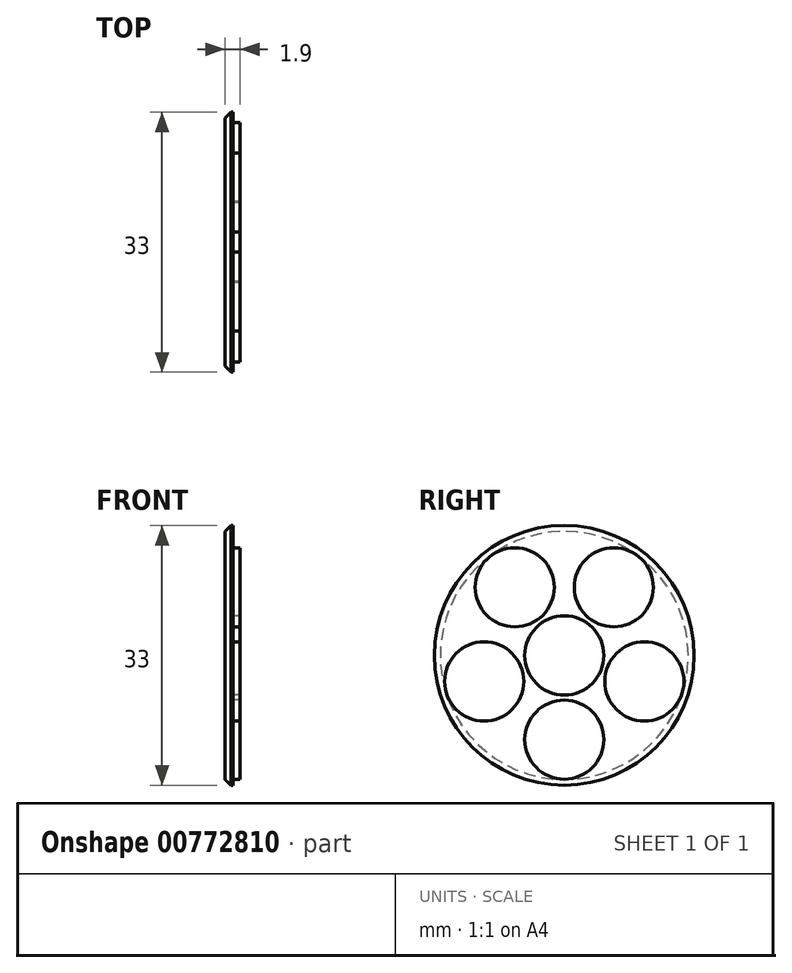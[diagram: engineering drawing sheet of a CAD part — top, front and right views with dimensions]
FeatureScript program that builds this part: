
annotation { "Feature Type Name" : "Feature", "Feature Type Description" : "" }
export const myFeature = defineFeature(function(context is Context, id is Id, definition is map)
    precondition{}
    {
        {
            var Q0;
            Q0=qCreatedBy(makeId("Right.planeOp"),FACE);
            var sketch = newSketch(context, id + "F0", { "sketchPlane" : qUnion([Q0])});
            skCircle(sketch, "E0.0", {"center": v(0, 0) * mm, "radius": 16.5 * mm});
            skSolve(sketch);
        }
        {
            var Q0;
            Q0 = qSketchRegion(id + "F0", true);
            extrude(context, id + "F1", {"entities" : qUnion([Q0]), "depth" : 1 * mm, "offsetDistance" : 25 * mm});
        }
        {
            var Q0;
            Q0=makeQuery(id+"F1.opExtrude","CAP_FACE",FACE,{"disambiguationData":[OSD([sQuery(id+"F0.wireOp",EDGE,"E0.0")])],"isStart":false});
            var sketch = newSketch(context, id + "F2", { "sketchPlane" : qUnion([Q0])});
            skCircle(sketch, "E1", {"center": v(0, 0) * mm, "radius": 5.03 * mm});
            skLineSegment(sketch, "E2", {"start": v(0, 0) * mm, "end": v(0, -10.7) * mm, "construction": true});
            skCircle(sketch, "E3", {"center": v(0, -10.7) * mm, "radius": 5.03 * mm});
            skCircle(sketch, "E4.1.0", {"center": v(10.18, -3.3) * mm, "radius": 5.03 * mm});
            skCircle(sketch, "E4.2.0", {"center": v(6.29, 8.66) * mm, "radius": 5.03 * mm});
            skCircle(sketch, "E4.3.0", {"center": v(-6.29, 8.66) * mm, "radius": 5.03 * mm});
            skCircle(sketch, "E4.4.0", {"center": v(-10.18, -3.3) * mm, "radius": 5.03 * mm});
            skSolve(sketch);
        }
        {
            var Q0;
            Q0 = qSketchRegion(id + "F2", true);
            extrude(context, id + "F3", {"entities" : qUnion([Q0]), "operationType" : NewBodyOperationType.ADD, "depth" : 0.9 * mm, "offsetDistance" : 25 * mm});
        }
        {
            var Q0;
            Q0=makeQuery(id+"F1.opExtrude","CAP_EDGE",EDGE,{"disambiguationData":[OSD([sQuery(id+"F0.wireOp",EDGE,"E0.0")])],"isStart":true});
            chamfer(context, id + "F4", {"entities" : qUnion([Q0]), "width" : 0.75 * mm, "tangentPropagation" : true});
        }
    });
